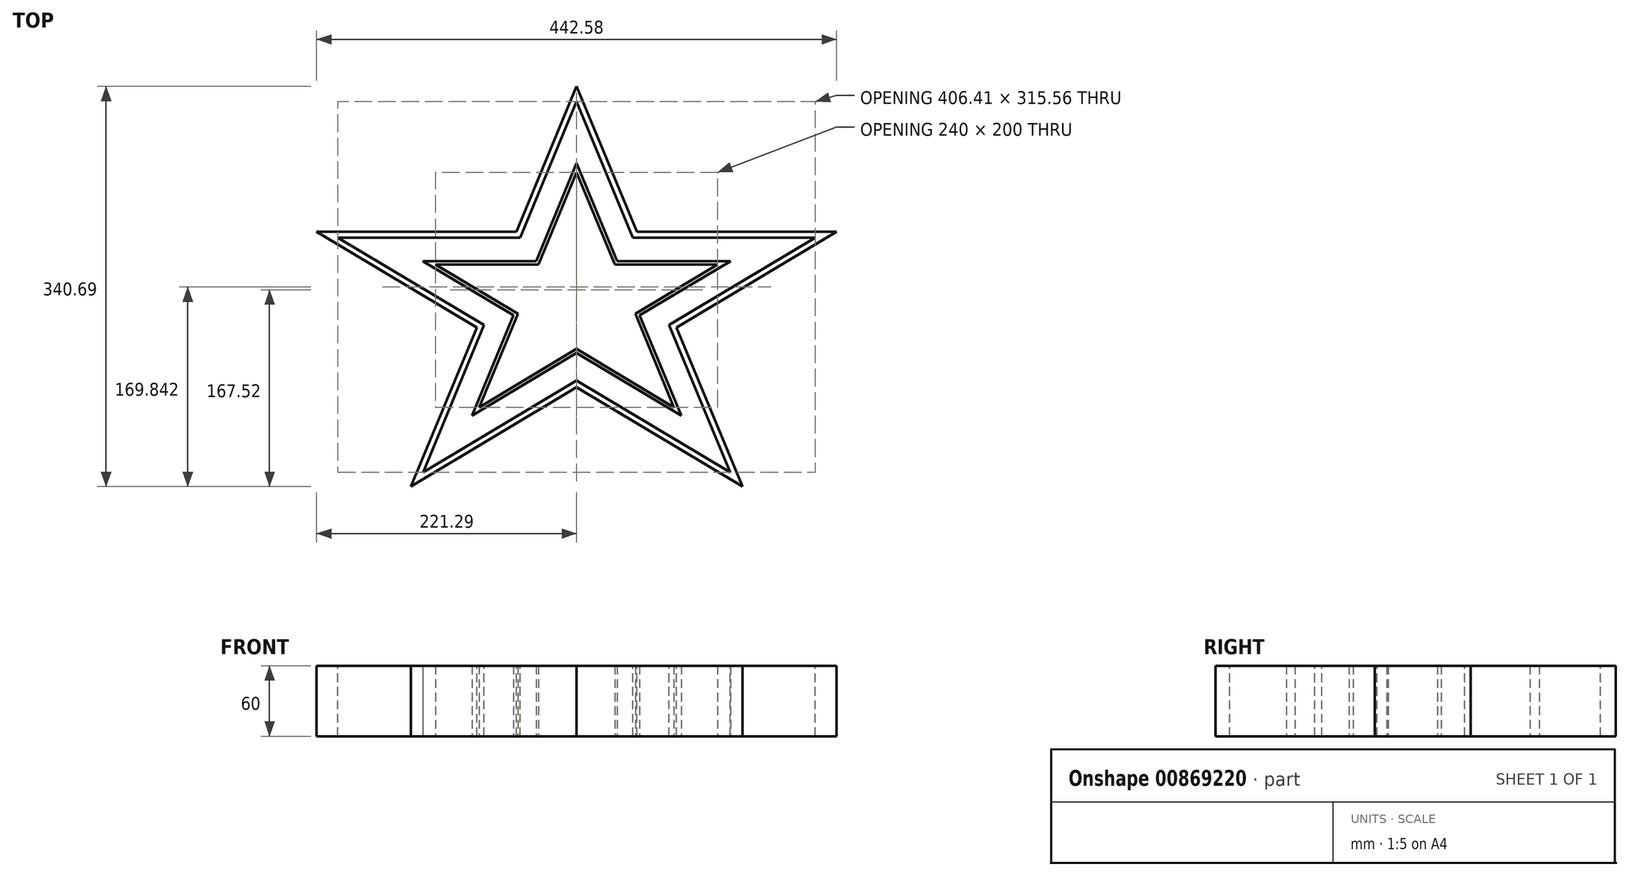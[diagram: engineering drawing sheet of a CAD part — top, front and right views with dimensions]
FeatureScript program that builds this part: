
annotation { "Feature Type Name" : "Feature", "Feature Type Description" : "" }
export const myFeature = defineFeature(function(context is Context, id is Id, definition is map)
    precondition{}
    {
        {
            var Q0;
            Q0=qCreatedBy(makeId("Top.planeOp"),FACE);
            var sketch = newSketch(context, id + "F0", { "sketchPlane" : qUnion([Q0])});
            skPoint(sketch, "E0.middle", {"position": v(0, 0) * mm});
            skPoint(sketch, "E1", {"position": v(0, 100) * mm});
            skLineSegment(sketch, "E2", {"start": v(0, 100) * mm, "end": v(-32.55, 21.42) * mm});
            skLineSegment(sketch, "E3", {"start": v(0, 100) * mm, "end": v(32.55, 21.42) * mm});
            skLineSegment(sketch, "E4", {"start": v(-120, 21.42) * mm, "end": v(-32.55, 21.42) * mm});
            skLineSegment(sketch, "E5", {"start": v(-120, 21.42) * mm, "end": v(-49.92, -20.53) * mm});
            skLineSegment(sketch, "E6", {"start": v(120, 21.42) * mm, "end": v(49.92, -20.53) * mm});
            skLineSegment(sketch, "E7.trimOffspring", {"start": v(-49.92, -20.53) * mm, "end": v(-82.84, -100) * mm});
            skLineSegment(sketch, "E8.trimOffspring", {"start": v(49.92, -20.53) * mm, "end": v(82.84, -100) * mm});
            skLineSegment(sketch, "E9.trimOffspring", {"start": v(32.55, 21.42) * mm, "end": v(120, 21.42) * mm});
            skLineSegment(sketch, "E10.trimOffspring", {"start": v(0, -50.41) * mm, "end": v(82.84, -100) * mm});
            skLineSegment(sketch, "E11.trimOffspring", {"start": v(0, -50.41) * mm, "end": v(-82.84, -100) * mm});
            skLineSegment(sketch, "E12.0", {"start": v(0, -53.9) * mm, "end": v(89.09, -107.23) * mm});
            skLineSegment(sketch, "E12.1", {"start": v(53.69, -21.77) * mm, "end": v(89.09, -107.23) * mm});
            skLineSegment(sketch, "E12.2", {"start": v(0, -53.9) * mm, "end": v(-89.09, -107.23) * mm});
            skLineSegment(sketch, "E12.3", {"start": v(130.85, 24.42) * mm, "end": v(53.69, -21.77) * mm});
            skLineSegment(sketch, "E12.4", {"start": v(34.55, 24.42) * mm, "end": v(130.85, 24.42) * mm});
            skLineSegment(sketch, "E12.5", {"start": v(0, 107.84) * mm, "end": v(34.55, 24.42) * mm});
            skLineSegment(sketch, "E12.6", {"start": v(-53.69, -21.77) * mm, "end": v(-89.09, -107.23) * mm});
            skLineSegment(sketch, "E12.7", {"start": v(-130.85, 24.42) * mm, "end": v(-53.69, -21.77) * mm});
            skLineSegment(sketch, "E12.8", {"start": v(-130.85, 24.42) * mm, "end": v(-34.55, 24.42) * mm});
            skLineSegment(sketch, "E12.9", {"start": v(0, 107.84) * mm, "end": v(-34.55, 24.42) * mm});
            skSolve(sketch);
        }
        {
            var Q0;
            Q0=makeQuery(id+"F0.imprint","IMPRINT",FACE,{"disambiguationData":[TD([[makeQuery(id+"F0.imprint","IMPRINT",EDGE,{"derivedFrom":sQuery(id+"F0.wireOp",EDGE,"E2")}),-1.0]])]});
            extrude(context, id + "F1", {"entities" : qUnion([Q0]), "depth" : 60 * mm, "offsetDistance" : 25 * mm});
        }
        {
            var Q0;
            Q0=makeQuery(id+"F1.opExtrude","CAP_FACE",FACE,{"disambiguationData":[OSD([sQuery(id+"F0.wireOp",EDGE,"E2"),sQuery(id+"F0.wireOp",EDGE,"E3"),sQuery(id+"F0.wireOp",EDGE,"E4"),sQuery(id+"F0.wireOp",EDGE,"E5"),sQuery(id+"F0.wireOp",EDGE,"E6"),sQuery(id+"F0.wireOp",EDGE,"E7.trimOffspring"),sQuery(id+"F0.wireOp",EDGE,"E8.trimOffspring"),sQuery(id+"F0.wireOp",EDGE,"E9.trimOffspring"),sQuery(id+"F0.wireOp",EDGE,"E10.trimOffspring"),sQuery(id+"F0.wireOp",EDGE,"E11.trimOffspring"),sQuery(id+"F0.wireOp",EDGE,"E12.0"),sQuery(id+"F0.wireOp",EDGE,"E12.1"),sQuery(id+"F0.wireOp",EDGE,"E12.2"),sQuery(id+"F0.wireOp",EDGE,"E12.3"),sQuery(id+"F0.wireOp",EDGE,"E12.4"),sQuery(id+"F0.wireOp",EDGE,"E12.5"),sQuery(id+"F0.wireOp",EDGE,"E12.6"),sQuery(id+"F0.wireOp",EDGE,"E12.7"),sQuery(id+"F0.wireOp",EDGE,"E12.8"),sQuery(id+"F0.wireOp",EDGE,"E12.9")])],"isStart":false});
            var sketch = newSketch(context, id + "F2", { "sketchPlane" : qUnion([Q0])});
            skLineSegment(sketch, "E13.0", {"start": v(0, 160.1) * mm, "end": v(47.92, 44.42) * mm});
            skLineSegment(sketch, "E13.1", {"start": v(47.92, 44.42) * mm, "end": v(203.2, 44.42) * mm});
            skLineSegment(sketch, "E13.2", {"start": v(0, 160.1) * mm, "end": v(-47.92, 44.42) * mm});
            skLineSegment(sketch, "E13.3", {"start": v(203.2, 44.42) * mm, "end": v(78.77, -30.06) * mm});
            skLineSegment(sketch, "E13.4", {"start": v(78.77, -30.06) * mm, "end": v(130.7, -155.46) * mm});
            skLineSegment(sketch, "E13.5", {"start": v(0, -77.22) * mm, "end": v(130.7, -155.46) * mm});
            skLineSegment(sketch, "E13.6", {"start": v(-203.2, 44.42) * mm, "end": v(-47.92, 44.42) * mm});
            skLineSegment(sketch, "E13.7", {"start": v(-203.2, 44.42) * mm, "end": v(-78.77, -30.06) * mm});
            skLineSegment(sketch, "E13.8", {"start": v(-78.77, -30.06) * mm, "end": v(-130.7, -155.46) * mm});
            skLineSegment(sketch, "E13.9", {"start": v(0, -77.22) * mm, "end": v(-130.7, -155.46) * mm});
            skLineSegment(sketch, "E14.0", {"start": v(0, 173.17) * mm, "end": v(51.26, 49.42) * mm});
            skLineSegment(sketch, "E14.1", {"start": v(51.26, 49.42) * mm, "end": v(221.3, 49.42) * mm});
            skLineSegment(sketch, "E14.2", {"start": v(0, 173.17) * mm, "end": v(-51.26, 49.42) * mm});
            skLineSegment(sketch, "E14.3", {"start": v(221.3, 49.42) * mm, "end": v(85.04, -32.14) * mm});
            skLineSegment(sketch, "E14.4", {"start": v(85.04, -32.14) * mm, "end": v(141.12, -167.52) * mm});
            skLineSegment(sketch, "E14.5", {"start": v(0, -83.04) * mm, "end": v(141.12, -167.52) * mm});
            skLineSegment(sketch, "E14.6", {"start": v(-221.3, 49.42) * mm, "end": v(-51.26, 49.42) * mm});
            skLineSegment(sketch, "E14.7", {"start": v(-221.3, 49.42) * mm, "end": v(-85.04, -32.14) * mm});
            skLineSegment(sketch, "E14.8", {"start": v(-85.04, -32.14) * mm, "end": v(-141.12, -167.52) * mm});
            skLineSegment(sketch, "E14.9", {"start": v(0, -83.04) * mm, "end": v(-141.12, -167.52) * mm});
            skSolve(sketch);
        }
        {
            var Q0;
            Q0=makeQuery(id+"F2.imprint","IMPRINT",FACE,{"disambiguationData":[TD([[makeQuery(id+"F2.imprint","IMPRINT",EDGE,{"derivedFrom":sQuery(id+"F2.wireOp",EDGE,"E13.0")}),1.0]])]});
            extrude(context, id + "F3", {"entities" : qUnion([Q0]), "oppositeDirection" : true, "depth" : 60 * mm, "offsetDistance" : 25 * mm});
        }
    });
